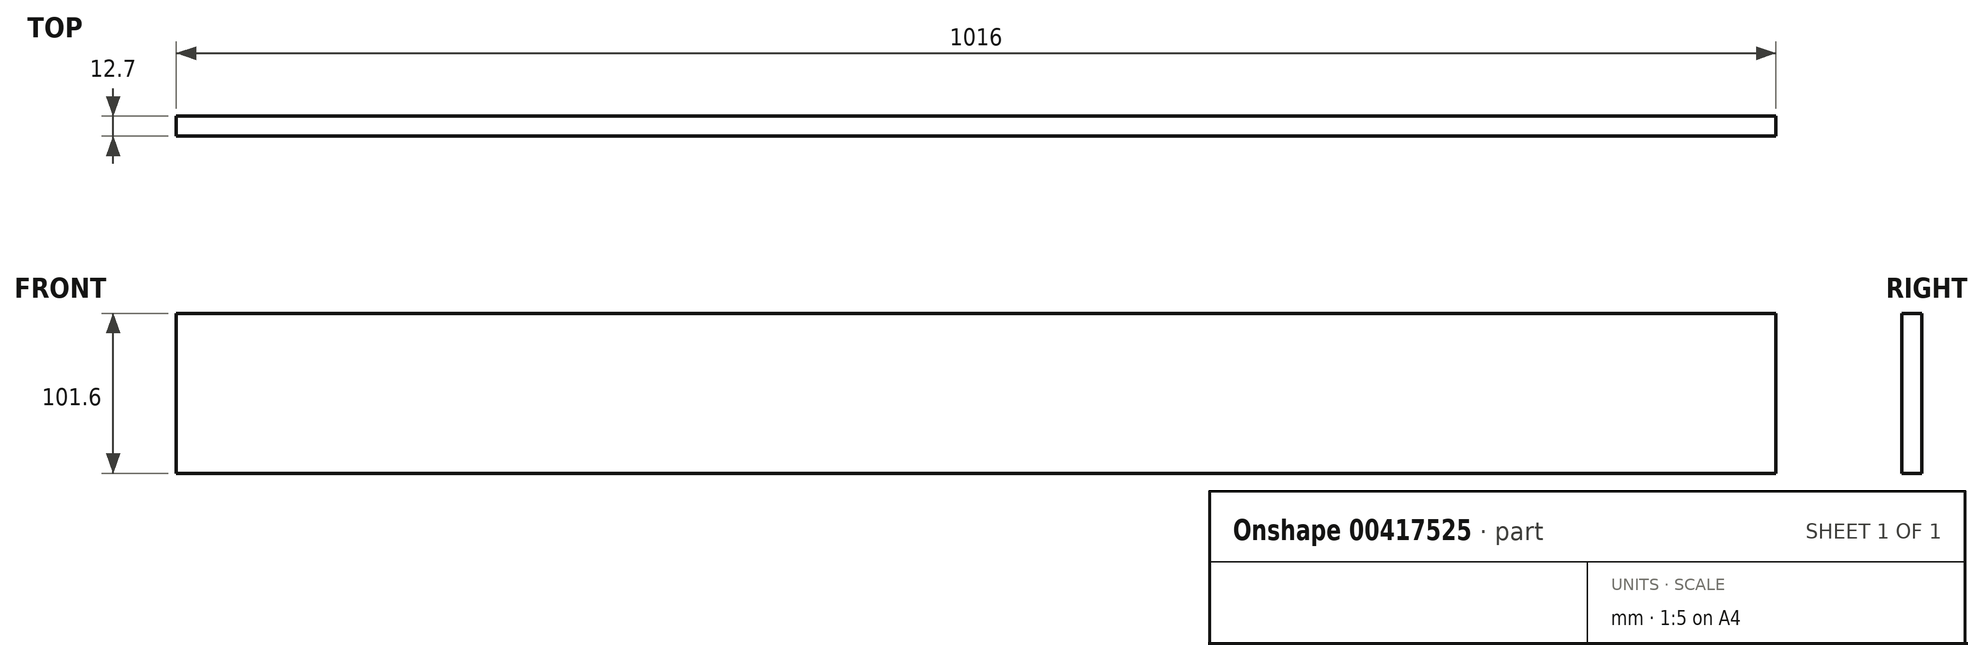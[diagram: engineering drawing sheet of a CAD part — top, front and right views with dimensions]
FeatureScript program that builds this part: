
annotation { "Feature Type Name" : "Feature", "Feature Type Description" : "" }
export const myFeature = defineFeature(function(context is Context, id is Id, definition is map)
    precondition{}
    {
        {
            var Q0;
            Q0=qCreatedBy(makeId("Front.planeOp"),FACE);
            var sketch = newSketch(context, id + "F0", { "sketchPlane" : qUnion([Q0])});
            skLineSegment(sketch, "E0.bottom", {"start": v(-508, 50.8) * mm, "end": v(508, 50.8) * mm});
            skLineSegment(sketch, "E0.top", {"start": v(-508, -50.8) * mm, "end": v(508, -50.8) * mm});
            skLineSegment(sketch, "E0.left", {"start": v(-508, 50.8) * mm, "end": v(-508, -50.8) * mm});
            skLineSegment(sketch, "E0.right", {"start": v(508, 50.8) * mm, "end": v(508, -50.8) * mm});
            skPoint(sketch, "E0.middle", {"position": v(0, 0) * mm});
            skSolve(sketch);
        }
        {
            var Q0;
            Q0=makeQuery(id+"F0.imprint","IMPRINT",FACE,{"disambiguationData":[TD([[makeQuery(id+"F0.imprint","IMPRINT",EDGE,{"derivedFrom":sQuery(id+"F0.wireOp",EDGE,"E0.bottom")}),-1.0]])]});
            extrude(context, id + "F1", {"entities" : qUnion([Q0]), "depth" : 12.7 * mm});
        }
    });
